# Revit family: НЕВАТОМ_Вставка гибкая ВГ, Версия 1
name_source: partatom
category: Оборудование
revit_build: Autodesk Revit 2017 (Build: 20170118_1100(x64)
units: mm (PartAtom-declared; Revit-internal decimal feet)

## family parameters
Всегда вертикально = Да
На основе рабочей плоскости = Нет
Общий = Да
При загрузке вырезать с полостями = Нет
Размер круглого соединителя = Использовать диаметр
Тип детали = Нормальный
Точка расчета площади = Нет

## types (9) — shared parameters
ADSK_Единица измерения = шт.
ADSK_Завод-изготовитель = НЕВАТОМ
ADSK_Количество = 1
ADSK_Наименование = Гибкая вставка ВГ
t = 5 мм
Материал = Сталь ASTM A441

## per-type parameters (varying)
| type | A | A+5 | ADSK_Марка | B | B+5 | L | А+40 | В+40 |
| Вставка гибкая ВГ-400*200 | 400 мм | 405 мм | Вставка гибкая ВГ-400*200-У-О-ш2.ш2 | 200 мм | 205 мм | 140 мм | 440 мм | 240 мм |
| Вставка гибкая ВГ-500*250 | 500 мм | 505 мм | Вставка гибкая ВГ-500*250-У-О-ш2.ш2 | 250 мм | 255 мм | 140 мм | 540 мм | 290 мм |
| Вставка гибкая ВГ-500*300 | 500 мм | 505 мм | Вставка гибкая ВГ-500*300-У-О-ш2.ш2 | 300 мм | 305 мм | 140 мм | 540 мм | 340 мм |
| Вставка гибкая ВГ-600*300 | 600 мм | 605 мм | Вставка гибкая ВГ-600*300-У-О-ш2.ш2 | 300 мм | 305 мм | 140 мм | 640 мм | 340 мм |
| Вставка гибкая ВГ-600*350 | 600 мм | 605 мм | Вставка гибкая ВГ-600*350-У-О-ш2.ш2 | 350 мм | 355 мм | 140 мм | 640 мм | 390 мм |
| Вставка гибкая ВГ-700*400 | 700 мм | 705 мм | Вставка гибкая ВГ-700*400-У-О-ш2.ш2 | 400 мм | 405 мм | 240 мм | 740 мм | 440 мм |
| Вставка гибкая ВГ-800*500 | 800 мм | 805 мм | Вставка гибкая ВГ-800*500-У-О-ш2.ш2 | 500 мм | 505 мм | 240 мм | 840 мм | 540 мм |
| Вставка гибкая ВГ-900*500 | 900 мм | 905 мм | Вставка гибкая ВГ-900*500-У-О-ш2.ш2 | 500 мм | 505 мм | 240 мм | 940 мм | 540 мм |
| Вставка гибкая ВГ-1000*500 | 1000 мм | 1005 мм | Вставка гибкая ВГ-1000*500-У-О-ш2.ш2 | 500 мм | 505 мм | 240 мм | 1040 мм | 540 мм |
